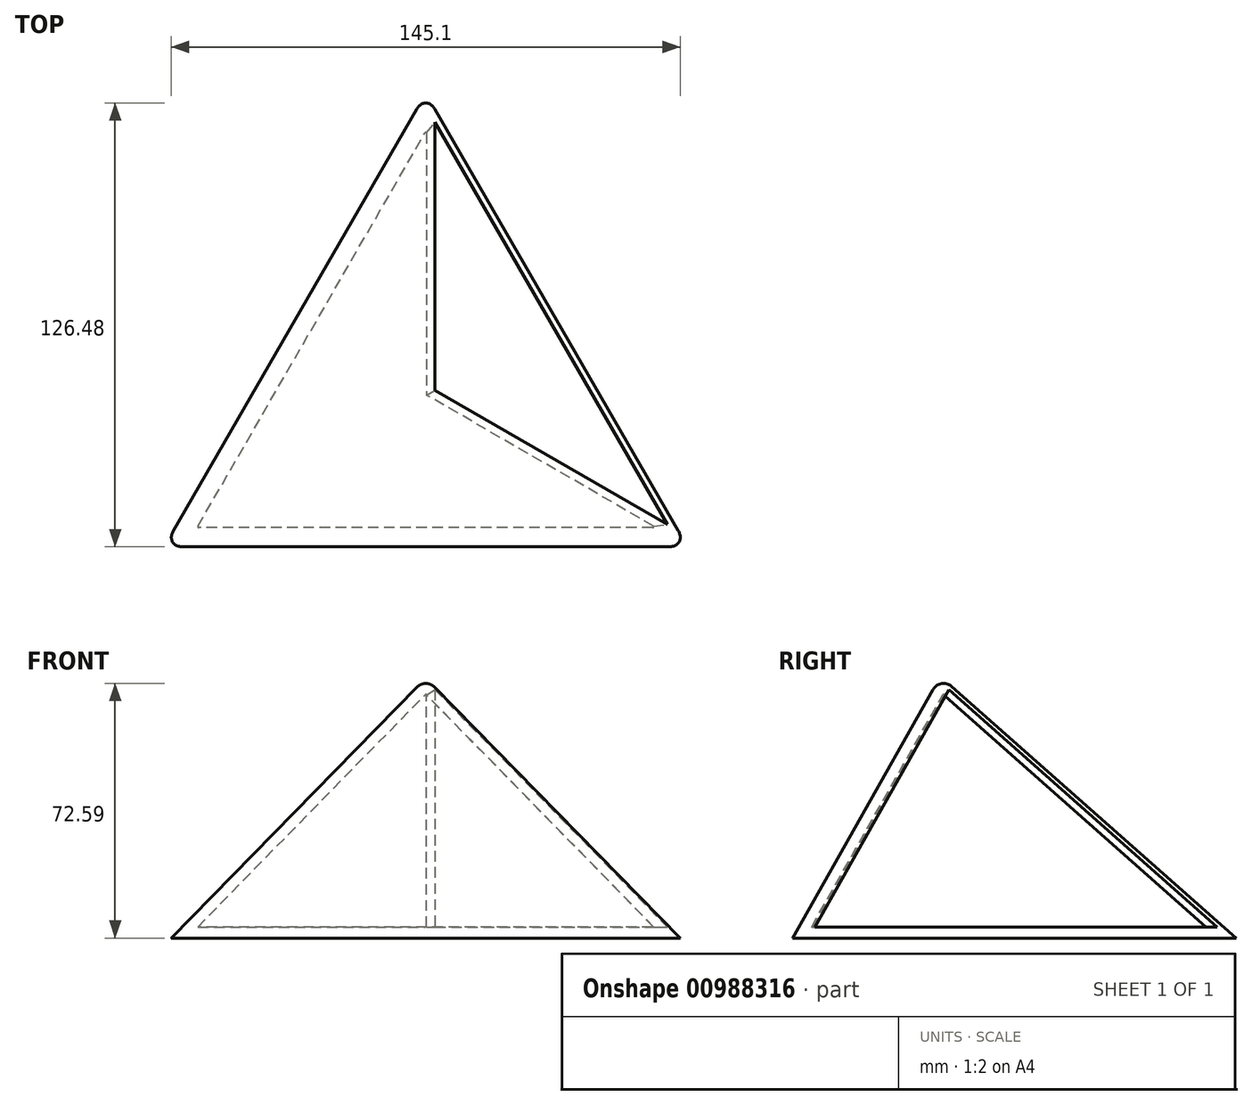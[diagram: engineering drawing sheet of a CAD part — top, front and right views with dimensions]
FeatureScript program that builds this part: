
annotation { "Feature Type Name" : "Feature", "Feature Type Description" : "" }
export const myFeature = defineFeature(function(context is Context, id is Id, definition is map)
    precondition{}
    {
        {
            var Q0;
            Q0=qCreatedBy(makeId("Top.planeOp"),FACE);
            var sketch = newSketch(context, id + "F0", { "sketchPlane" : qUnion([Q0])});
            skCircle(sketch, "E0.cCircle", {"center": v(0, 0) * mm, "radius": 86.16 * mm, "construction": true});
            skLineSegment(sketch, "E0.0", {"start": v(0, 86.16) * mm, "end": v(74.61, -43.08) * mm});
            skLineSegment(sketch, "E0.1", {"start": v(74.61, -43.08) * mm, "end": v(-74.61, -43.08) * mm});
            skLineSegment(sketch, "E0.2", {"start": v(-74.61, -43.08) * mm, "end": v(0, 86.16) * mm});
            skSolve(sketch);
        }
        {
            var Q0;
            Q0=qCreatedBy(makeId("Top.planeOp"),FACE);
            cPlane(context, id + "F1", {"entities" : qUnion([Q0]), "cplaneType" : CPlaneType.OFFSET, "offset" : (25.4 * 3) * mm, "width" : 150 * mm, "height" : 150 * mm});
        }
        {
            var Q0;
            Q0=qCreatedBy(id+"F1.planeOp",FACE);
            var sketch = newSketch(context, id + "F2", { "sketchPlane" : qUnion([Q0])});
            skPoint(sketch, "E1", {"position": v(0, 0) * mm});
            skSolve(sketch);
        }
        {
            var Q0;
            Q0=makeQuery(id+"F0.imprint","IMPRINT",FACE,{"disambiguationData":[TD([[makeQuery(id+"F0.imprint","IMPRINT",EDGE,{"derivedFrom":sQuery(id+"F0.wireOp",EDGE,"E0.0")}),-1.0]])]});
            var Q1;
            Q1=sQuery(id+"F2.wireOp",VERTEX,"E1");
            loft(context, id + "F3", {"sheetProfilesArray" : [{ "sheetProfileEntities" : qUnion([Q0]) }, { "sheetProfileEntities" : qUnion([Q1]) }]});
        }
        {
            var Q0;
            Q0=makeQuery(id+"F3.opLoft","SWEPT_EDGE",EDGE,{"disambiguationData":[OSD([sQuery(id+"F0.wireOp",EDGE,"E0.0"),sQuery(id+"F0.wireOp",EDGE,"E0.1"),sQuery(id+"F2.wireOp",VERTEX,"E1")])]});
            var Q1;
            Q1=makeQuery(id+"F3.opLoft","SWEPT_EDGE",EDGE,{"disambiguationData":[OSD([sQuery(id+"F0.wireOp",EDGE,"E0.0"),sQuery(id+"F0.wireOp",EDGE,"E0.2"),sQuery(id+"F2.wireOp",VERTEX,"E1")])]});
            var Q2;
            Q2=makeQuery(id+"F3.opLoft","SWEPT_EDGE",EDGE,{"disambiguationData":[OSD([sQuery(id+"F0.wireOp",EDGE,"E0.1"),sQuery(id+"F0.wireOp",EDGE,"E0.2"),sQuery(id+"F2.wireOp",VERTEX,"E1")])]});
            fillet(context, id + "F4", {"entities" : qUnion([Q0, Q1, Q2]), "radius" : 3.5 * mm, "tangentPropagation" : true, "allowEdgeOverflow" : false});
        }
        {
            var Q0;
            {var subQ0=sQuery(id+"F0.wireOp",EDGE,"E0.0");var subQ1=sQuery(id+"F0.wireOp",EDGE,"E0.1");var subQ2=sQuery(id+"F0.wireOp",EDGE,"E0.2");Q0=makeQuery(id+"F3.opLoft","SWEPT_FACE",FACE,{"disambiguationData":[OSD([subQ0,subQ1,subQ2]),TDD([makeQuery(id+"F0.imprint","INTERSECT",VERTEX,{"derivedFrom":[subQ0,subQ2]}),makeQuery(id+"F0.imprint","INTERSECT",VERTEX,{"derivedFrom":[subQ0,subQ1]}),makeQuery(id+"F0.imprint","IMPRINT",EDGE,{"derivedFrom":subQ0})])]});}
            shell(context, id + "F5", {"entities" : qUnion([Q0]), "thickness" : 3.17 * mm});
        }
    });
